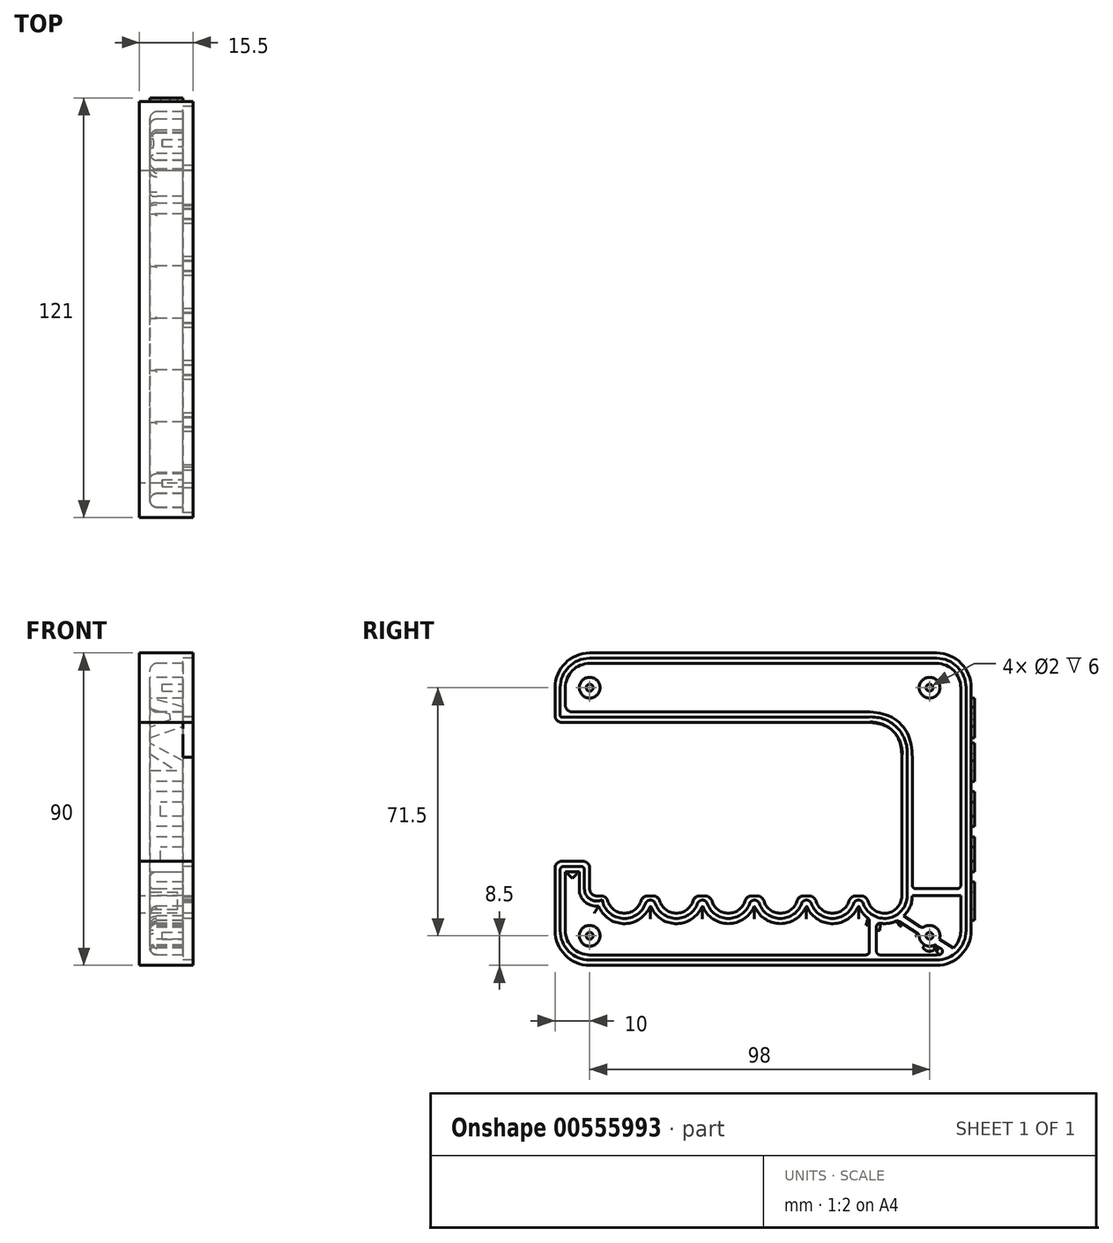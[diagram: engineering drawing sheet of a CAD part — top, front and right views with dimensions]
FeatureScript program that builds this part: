
annotation { "Feature Type Name" : "Feature", "Feature Type Description" : "" }
export const myFeature = defineFeature(function(context is Context, id is Id, definition is map)
    precondition{}
    {
        {
            var Q0;
            Q0=qCreatedBy(makeId("Right.planeOp"),FACE);
            var sketch = newSketch(context, id + "F0", { "sketchPlane" : qUnion([Q0])});
            skLineSegment(sketch, "E0", {"start": v(-120, 0) * mm, "end": v(0, 0) * mm});
            skLineSegment(sketch, "E1", {"start": v(0, 0) * mm, "end": v(0, 90) * mm});
            skLineSegment(sketch, "E2", {"start": v(0, 90) * mm, "end": v(-120, 90) * mm});
            skLineSegment(sketch, "E3", {"start": v(-120, 90) * mm, "end": v(-120, 70) * mm});
            skLineSegment(sketch, "E4", {"start": v(-120, 70) * mm, "end": v(-20, 70) * mm});
            skLineSegment(sketch, "E5", {"start": v(-20, 70) * mm, "end": v(-20, 20) * mm});
            skLineSegment(sketch, "E6", {"start": v(-120, 0) * mm, "end": v(-120, 30) * mm});
            skLineSegment(sketch, "E7", {"start": v(-120, 30) * mm, "end": v(-110, 30) * mm});
            skLineSegment(sketch, "E8", {"start": v(-110, 30) * mm, "end": v(-110, 20) * mm});
            skPoint(sketch, "E9.orphan", {"position": v(-120, 20) * mm});
            skLineSegment(sketch, "E10", {"start": v(-110, 20) * mm, "end": v(-105, 20) * mm});
            skArc(sketch, "E11", {"start": v(-105, 20) * mm, "mid": v(-100, 15) * mm, "end": v(-95, 20) * mm});
            skLineSegment(sketch, "E12", {"start": v(-95, 20) * mm, "end": v(-90, 20) * mm});
            skArc(sketch, "E13", {"start": v(-90, 20) * mm, "mid": v(-85, 15) * mm, "end": v(-80, 20) * mm});
            skLineSegment(sketch, "E14", {"start": v(-80, 20) * mm, "end": v(-75, 20) * mm});
            skArc(sketch, "E15", {"start": v(-75, 20) * mm, "mid": v(-70, 15) * mm, "end": v(-65, 20) * mm});
            skLineSegment(sketch, "E16", {"start": v(-65, 20) * mm, "end": v(-60, 20) * mm});
            skArc(sketch, "E17", {"start": v(-60, 20) * mm, "mid": v(-55, 15) * mm, "end": v(-50, 20) * mm});
            skLineSegment(sketch, "E18", {"start": v(-50, 20) * mm, "end": v(-45, 20) * mm});
            skArc(sketch, "E19", {"start": v(-45, 20) * mm, "mid": v(-40, 15) * mm, "end": v(-35, 20) * mm});
            skLineSegment(sketch, "E20", {"start": v(-35, 20) * mm, "end": v(-30, 20) * mm});
            skArc(sketch, "E21", {"start": v(-30, 20) * mm, "mid": v(-25, 15) * mm, "end": v(-20, 20) * mm});
            skSolve(sketch);
        }
        {
            var Q0;
            Q0=makeQuery(id+"F0.imprint","IMPRINT",FACE,{"disambiguationData":[TD([[makeQuery(id+"F0.imprint","IMPRINT",EDGE,{"derivedFrom":sQuery(id+"F0.wireOp",EDGE,"E0")}),1.0]])]});
            extrude(context, id + "F1", {"entities" : qUnion([Q0]), "depth" : 12.5 * mm, "offsetDistance" : 25 * mm});
        }
        {
            var Q0;
            Q0=makeQuery(id+"F1.opExtrude","SWEPT_EDGE",EDGE,{"disambiguationData":[OSD([sQuery(id+"F0.wireOp",EDGE,"E2"),sQuery(id+"F0.wireOp",EDGE,"E3")])]});
            var Q1;
            Q1=makeQuery(id+"F1.opExtrude","SWEPT_EDGE",EDGE,{"disambiguationData":[OSD([sQuery(id+"F0.wireOp",EDGE,"E1"),sQuery(id+"F0.wireOp",EDGE,"E2")])]});
            var Q2;
            Q2=makeQuery(id+"F1.opExtrude","SWEPT_EDGE",EDGE,{"disambiguationData":[OSD([sQuery(id+"F0.wireOp",EDGE,"E0"),sQuery(id+"F0.wireOp",EDGE,"E1")])]});
            var Q3;
            Q3=makeQuery(id+"F1.opExtrude","SWEPT_EDGE",EDGE,{"disambiguationData":[OSD([sQuery(id+"F0.wireOp",EDGE,"E0"),sQuery(id+"F0.wireOp",EDGE,"E6")])]});
            fillet(context, id + "F2", {"entities" : qUnion([Q0, Q1, Q2, Q3]), "radius" : 10 * mm, "tangentPropagation" : true, "allowEdgeOverflow" : false});
        }
        {
            var Q0;
            Q0=makeQuery(id+"F1.opExtrude","SWEPT_EDGE",EDGE,{"disambiguationData":[OSD([sQuery(id+"F0.wireOp",EDGE,"E4"),sQuery(id+"F0.wireOp",EDGE,"E5")])]});
            fillet(context, id + "F3", {"entities" : qUnion([Q0]), "radius" : 10 * mm, "tangentPropagation" : true, "rho" : 0.5, "crossSection" : FilletCrossSection.CONIC, "allowEdgeOverflow" : false});
        }
        {
            var Q0;
            Q0=makeQuery(id+"F1.opExtrude","SWEPT_EDGE",EDGE,{"disambiguationData":[OSD([sQuery(id+"F0.wireOp",EDGE,"E6"),sQuery(id+"F0.wireOp",EDGE,"E7")])]});
            var Q1;
            Q1=makeQuery(id+"F1.opExtrude","SWEPT_EDGE",EDGE,{"disambiguationData":[OSD([sQuery(id+"F0.wireOp",EDGE,"E7"),sQuery(id+"F0.wireOp",EDGE,"E8")])]});
            var Q2;
            Q2=makeQuery(id+"F1.opExtrude","SWEPT_EDGE",EDGE,{"disambiguationData":[OSD([sQuery(id+"F0.wireOp",EDGE,"E8"),sQuery(id+"F0.wireOp",EDGE,"E10")])]});
            var Q3;
            Q3=makeQuery(id+"F1.opExtrude","SWEPT_EDGE",EDGE,{"disambiguationData":[OSD([sQuery(id+"F0.wireOp",EDGE,"E10"),sQuery(id+"F0.wireOp",EDGE,"E11")])]});
            var Q4;
            Q4=makeQuery(id+"F1.opExtrude","SWEPT_EDGE",EDGE,{"disambiguationData":[OSD([sQuery(id+"F0.wireOp",EDGE,"E11"),sQuery(id+"F0.wireOp",EDGE,"E12")])]});
            var Q5;
            Q5=makeQuery(id+"F1.opExtrude","SWEPT_EDGE",EDGE,{"disambiguationData":[OSD([sQuery(id+"F0.wireOp",EDGE,"E12"),sQuery(id+"F0.wireOp",EDGE,"E13")])]});
            var Q6;
            Q6=makeQuery(id+"F1.opExtrude","SWEPT_EDGE",EDGE,{"disambiguationData":[OSD([sQuery(id+"F0.wireOp",EDGE,"E13"),sQuery(id+"F0.wireOp",EDGE,"E14")])]});
            var Q7;
            Q7=makeQuery(id+"F1.opExtrude","SWEPT_EDGE",EDGE,{"disambiguationData":[OSD([sQuery(id+"F0.wireOp",EDGE,"E14"),sQuery(id+"F0.wireOp",EDGE,"E15")])]});
            var Q8;
            Q8=makeQuery(id+"F1.opExtrude","SWEPT_EDGE",EDGE,{"disambiguationData":[OSD([sQuery(id+"F0.wireOp",EDGE,"E15"),sQuery(id+"F0.wireOp",EDGE,"E16")])]});
            var Q9;
            Q9=makeQuery(id+"F1.opExtrude","SWEPT_EDGE",EDGE,{"disambiguationData":[OSD([sQuery(id+"F0.wireOp",EDGE,"E16"),sQuery(id+"F0.wireOp",EDGE,"E17")])]});
            var Q10;
            Q10=makeQuery(id+"F1.opExtrude","SWEPT_EDGE",EDGE,{"disambiguationData":[OSD([sQuery(id+"F0.wireOp",EDGE,"E17"),sQuery(id+"F0.wireOp",EDGE,"E18")])]});
            var Q11;
            Q11=makeQuery(id+"F1.opExtrude","SWEPT_EDGE",EDGE,{"disambiguationData":[OSD([sQuery(id+"F0.wireOp",EDGE,"E18"),sQuery(id+"F0.wireOp",EDGE,"E19")])]});
            var Q12;
            Q12=makeQuery(id+"F1.opExtrude","SWEPT_EDGE",EDGE,{"disambiguationData":[OSD([sQuery(id+"F0.wireOp",EDGE,"E19"),sQuery(id+"F0.wireOp",EDGE,"E20")])]});
            var Q13;
            Q13=makeQuery(id+"F1.opExtrude","SWEPT_EDGE",EDGE,{"disambiguationData":[OSD([sQuery(id+"F0.wireOp",EDGE,"E20"),sQuery(id+"F0.wireOp",EDGE,"E21")])]});
            fillet(context, id + "F4", {"entities" : qUnion([Q0, Q1, Q2, Q3, Q4, Q5, Q6, Q7, Q8, Q9, Q10, Q11, Q12, Q13]), "radius" : 2 * mm, "tangentPropagation" : true, "allowEdgeOverflow" : false});
        }
        {
            var Q0;
            Q0=makeQuery(id+"F1.opExtrude","SWEPT_FACE",FACE,{"disambiguationData":[OSD([sQuery(id+"F0.wireOp",EDGE,"E1")])]});
            var sketch = newSketch(context, id + "F5", { "sketchPlane" : qUnion([Q0])});
            skLineSegment(sketch, "E22.bottom", {"start": v(-12.5, 13) * mm, "end": v(-3, 13) * mm, "construction": true});
            skLineSegment(sketch, "E22.top", {"start": v(-12.5, 77) * mm, "end": v(-3, 77) * mm, "construction": true});
            skLineSegment(sketch, "E22.right", {"start": v(-3, 13) * mm, "end": v(-3, 77) * mm, "construction": true});
            skLineSegment(sketch, "E23.bottom", {"start": v(-12.5, 13) * mm, "end": v(-3, 13) * mm});
            skLineSegment(sketch, "E23.right", {"start": v(-3, 13) * mm, "end": v(-3, 16) * mm});
            skLineSegment(sketch, "E24.right", {"start": v(-11, 16) * mm, "end": v(-11, 21) * mm});
            skLineSegment(sketch, "E25.top", {"start": v(-12.5, 24) * mm, "end": v(-3, 24) * mm});
            skLineSegment(sketch, "E25.right", {"start": v(-3, 21) * mm, "end": v(-3, 24) * mm});
            skLineSegment(sketch, "E26.trimOffspring", {"start": v(-11, 21) * mm, "end": v(-3, 21) * mm});
            skLineSegment(sketch, "E27.trimOffspring", {"start": v(-11, 16) * mm, "end": v(-3, 16) * mm});
            skLineSegment(sketch, "E28.top", {"start": v(-12.5, 37) * mm, "end": v(-3, 37) * mm});
            skLineSegment(sketch, "E28.right", {"start": v(-3, 27) * mm, "end": v(-3, 37) * mm});
            skLineSegment(sketch, "E29.bottom", {"start": v(-12.5, 40) * mm, "end": v(-3, 40) * mm});
            skLineSegment(sketch, "E29.top", {"start": v(-12.5, 50) * mm, "end": v(-3, 50) * mm});
            skLineSegment(sketch, "E29.right", {"start": v(-3, 40) * mm, "end": v(-3, 50) * mm});
            skLineSegment(sketch, "E30.bottom", {"start": v(-12.5, 30) * mm, "end": v(-6, 30) * mm});
            skLineSegment(sketch, "E30.top", {"start": v(-12.5, 34) * mm, "end": v(-6, 34) * mm});
            skLineSegment(sketch, "E30.right", {"start": v(-6, 30) * mm, "end": v(-6, 34) * mm});
            skLineSegment(sketch, "E31.bottom", {"start": v(-12.5, 43) * mm, "end": v(-6, 43) * mm});
            skLineSegment(sketch, "E31.top", {"start": v(-12.5, 47) * mm, "end": v(-6, 47) * mm});
            skLineSegment(sketch, "E31.right", {"start": v(-6, 43) * mm, "end": v(-6, 47) * mm});
            skLineSegment(sketch, "E32.bottom", {"start": v(-12.5, 53) * mm, "end": v(-3, 53) * mm});
            skLineSegment(sketch, "E32.right", {"start": v(-3, 53) * mm, "end": v(-3, 56) * mm});
            skLineSegment(sketch, "E33", {"start": v(-12.5, 59) * mm, "end": v(-3, 64) * mm});
            skLineSegment(sketch, "E34", {"start": v(-3, 64) * mm, "end": v(-3, 61) * mm});
            skLineSegment(sketch, "E35", {"start": v(-3, 65.61) * mm, "end": v(-12.5, 68.8) * mm});
            skLineSegment(sketch, "E36", {"start": v(-12.5, 74.5) * mm, "end": v(-3, 77) * mm});
            skLineSegment(sketch, "E37", {"start": v(-8.81, 70.73) * mm, "end": v(-3, 68.61) * mm});
            skLineSegment(sketch, "E38", {"start": v(-3, 68.61) * mm, "end": v(-3, 65.61) * mm});
            skLineSegment(sketch, "E39", {"start": v(-3, 77) * mm, "end": v(-3, 74) * mm});
            skLineSegment(sketch, "E40", {"start": v(-3, 74) * mm, "end": v(-8.57, 72.5) * mm});
            skLineSegment(sketch, "E41", {"start": v(-8.57, 72.5) * mm, "end": v(-8.81, 70.73) * mm});
            skLineSegment(sketch, "E42", {"start": v(-3, 61) * mm, "end": v(-10.73, 56) * mm});
            skLineSegment(sketch, "E43.trimOffspring", {"start": v(-10.73, 56) * mm, "end": v(-3, 56) * mm});
            skLineSegment(sketch, "E44", {"start": v(-12.5, 74.5) * mm, "end": v(-12.5, 68.8) * mm});
            skLineSegment(sketch, "E45.trimOffspring", {"start": v(-12.5, 59) * mm, "end": v(-12.5, 53) * mm});
            skPoint(sketch, "E32.top.end.orphan", {"position": v(-12.5, 56) * mm});
            skPoint(sketch, "E25.bottom.end.orphan", {"position": v(-14, 21) * mm});
            skLineSegment(sketch, "E46", {"start": v(-3, 27) * mm, "end": v(-12.5, 27) * mm});
            skLineSegment(sketch, "E47.trimOffspring", {"start": v(-12.5, 24) * mm, "end": v(-12.5, 13) * mm});
            skLineSegment(sketch, "E48.trimOffspring", {"start": v(-12.5, 30) * mm, "end": v(-12.5, 27) * mm});
            skLineSegment(sketch, "E49.trimOffspring", {"start": v(-12.5, 37) * mm, "end": v(-12.5, 34) * mm});
            skLineSegment(sketch, "E50.trimOffspring", {"start": v(-12.5, 43) * mm, "end": v(-12.5, 40) * mm});
            skLineSegment(sketch, "E51.trimOffspring", {"start": v(-12.5, 50) * mm, "end": v(-12.5, 47) * mm});
            skSolve(sketch);
        }
        {
            var Q0;
            Q0 = qSketchRegion(id + "F5", true);
            extrude(context, id + "F6", {"entities" : qUnion([Q0]), "operationType" : NewBodyOperationType.ADD, "depth" : 1 * mm, "offsetDistance" : 25 * mm});
        }
        {
            var Q0;
            Q0=makeQuery(id+"F6.boolean.opBoolean","MERGE",FACE,{"derivedFrom":[makeQuery(id+"F1.opExtrude","CAP_FACE",FACE,{"disambiguationData":[OSD([sQuery(id+"F0.wireOp",EDGE,"E0"),sQuery(id+"F0.wireOp",EDGE,"E1"),sQuery(id+"F0.wireOp",EDGE,"E2"),sQuery(id+"F0.wireOp",EDGE,"E3"),sQuery(id+"F0.wireOp",EDGE,"E4"),sQuery(id+"F0.wireOp",EDGE,"E5"),sQuery(id+"F0.wireOp",EDGE,"E6"),sQuery(id+"F0.wireOp",EDGE,"E7"),sQuery(id+"F0.wireOp",EDGE,"E8"),sQuery(id+"F0.wireOp",EDGE,"E10"),sQuery(id+"F0.wireOp",EDGE,"E11"),sQuery(id+"F0.wireOp",EDGE,"E12"),sQuery(id+"F0.wireOp",EDGE,"E13"),sQuery(id+"F0.wireOp",EDGE,"E14"),sQuery(id+"F0.wireOp",EDGE,"E15"),sQuery(id+"F0.wireOp",EDGE,"E16"),sQuery(id+"F0.wireOp",EDGE,"E17"),sQuery(id+"F0.wireOp",EDGE,"E18"),sQuery(id+"F0.wireOp",EDGE,"E19"),sQuery(id+"F0.wireOp",EDGE,"E20"),sQuery(id+"F0.wireOp",EDGE,"E21")])],"isStart":false}),makeQuery(id+"F6.opExtrude","SWEPT_FACE",FACE,{"disambiguationData":[OSD([sQuery(id+"F5.wireOp",EDGE,"E44")])]}),makeQuery(id+"F6.opExtrude","SWEPT_FACE",FACE,{"disambiguationData":[OSD([sQuery(id+"F5.wireOp",EDGE,"E45.trimOffspring")])]}),makeQuery(id+"F6.opExtrude","SWEPT_FACE",FACE,{"disambiguationData":[OSD([sQuery(id+"F5.wireOp",EDGE,"E47.trimOffspring")])]}),makeQuery(id+"F6.opExtrude","SWEPT_FACE",FACE,{"disambiguationData":[OSD([sQuery(id+"F5.wireOp",EDGE,"E48.trimOffspring")])]}),makeQuery(id+"F6.opExtrude","SWEPT_FACE",FACE,{"disambiguationData":[OSD([sQuery(id+"F5.wireOp",EDGE,"E49.trimOffspring")])]}),makeQuery(id+"F6.opExtrude","SWEPT_FACE",FACE,{"disambiguationData":[OSD([sQuery(id+"F5.wireOp",EDGE,"E50.trimOffspring")])]}),makeQuery(id+"F6.opExtrude","SWEPT_FACE",FACE,{"disambiguationData":[OSD([sQuery(id+"F5.wireOp",EDGE,"E51.trimOffspring")])]})]});
            shell(context, id + "F7", {"entities" : qUnion([Q0]), "thickness" : 3 * mm});
        }
        {
            var Q0;
            Q0=makeQuery(id+"F1.opExtrude","SWEPT_EDGE",EDGE,{"disambiguationData":[OSD([sQuery(id+"F0.wireOp",EDGE,"E3"),sQuery(id+"F0.wireOp",EDGE,"E4")])]});
            fillet(context, id + "F8", {"entities" : qUnion([Q0]), "radius" : 2 * mm, "tangentPropagation" : true, "allowEdgeOverflow" : false});
        }
        {
            var Q0;
            Q0=makeQuery(id+"F7.opShell","OFFSET_EDGE",EDGE,{"disambiguationData":[OSD([sQuery(id+"F0.wireOp",EDGE,"E3"),sQuery(id+"F0.wireOp",EDGE,"E4")])]});
            var Q1;
            {var subQ0=sQuery(id+"F0.wireOp",EDGE,"E4");Q1=makeQuery(id+"F7.opShell","OFFSET_EDGE",EDGE,{"disambiguationData":[OSD([subQ0]),TDD([makeQuery(id+"F1.opExtrude","CAP_EDGE",EDGE,{"disambiguationData":[OSD([subQ0])],"isStart":true})])]});}
            var Q2;
            {var subQ0=sQuery(id+"F0.wireOp",EDGE,"E21");var subQ1=sQuery(id+"F0.wireOp",EDGE,"E20");var subQ2=sQuery(id+"F0.wireOp",EDGE,"E19");var subQ3=sQuery(id+"F0.wireOp",EDGE,"E18");var subQ4=sQuery(id+"F0.wireOp",EDGE,"E17");var subQ5=sQuery(id+"F0.wireOp",EDGE,"E16");var subQ6=sQuery(id+"F0.wireOp",EDGE,"E15");var subQ7=sQuery(id+"F0.wireOp",EDGE,"E14");var subQ8=sQuery(id+"F0.wireOp",EDGE,"E13");var subQ9=sQuery(id+"F0.wireOp",EDGE,"E12");var subQ10=sQuery(id+"F0.wireOp",EDGE,"E11");var subQ11=sQuery(id+"F0.wireOp",EDGE,"E10");var subQ12=sQuery(id+"F0.wireOp",EDGE,"E8");var subQ13=sQuery(id+"F0.wireOp",EDGE,"E7");var subQ14=sQuery(id+"F0.wireOp",EDGE,"E6");var subQ15=sQuery(id+"F0.wireOp",EDGE,"E5");var subQ16=sQuery(id+"F0.wireOp",EDGE,"E4");var subQ17=sQuery(id+"F0.wireOp",EDGE,"E3");var subQ18=sQuery(id+"F0.wireOp",EDGE,"E2");var subQ19=sQuery(id+"F0.wireOp",EDGE,"E1");var subQ20=sQuery(id+"F0.wireOp",EDGE,"E0");Q2=makeQuery(id+"F7.opShell","OFFSET_EDGE",EDGE,{"disambiguationData":[OSD([subQ20,subQ19,subQ18,subQ17,subQ16,subQ15,subQ14,subQ13,subQ12,subQ11,subQ10,subQ9,subQ8,subQ7,subQ6,subQ5,subQ4,subQ3,subQ2,subQ1,subQ0]),TDD([makeQuery(id+"F3.opFillet","BLEND_EDGE",EDGE,{"blendedFrom":[makeQuery(id+"F1.opExtrude","SWEPT_EDGE",EDGE,{"disambiguationData":[OSD([subQ16,subQ15])]}),makeQuery(id+"F1.opExtrude","CAP_FACE",FACE,{"disambiguationData":[OSD([subQ20,subQ19,subQ18,subQ17,subQ16,subQ15,subQ14,subQ13,subQ12,subQ11,subQ10,subQ9,subQ8,subQ7,subQ6,subQ5,subQ4,subQ3,subQ2,subQ1,subQ0])],"isStart":true})],"blendedInto":[makeQuery(id+"F1.opExtrude","CAP_FACE",FACE,{"disambiguationData":[OSD([subQ20,subQ19,subQ18,subQ17,subQ16,subQ15,subQ14,subQ13,subQ12,subQ11,subQ10,subQ9,subQ8,subQ7,subQ6,subQ5,subQ4,subQ3,subQ2,subQ1,subQ0])],"isStart":true})]})])]});}
            var Q3;
            {var subQ0=sQuery(id+"F0.wireOp",EDGE,"E19");Q3=makeQuery(id+"F7.opShell","OFFSET_EDGE",EDGE,{"disambiguationData":[OSD([subQ0]),TDD([makeQuery(id+"F1.opExtrude","CAP_EDGE",EDGE,{"disambiguationData":[OSD([subQ0])],"isStart":true})])]});}
            var Q4;
            {var subQ0=sQuery(id+"F0.wireOp",EDGE,"E17");Q4=makeQuery(id+"F7.opShell","OFFSET_EDGE",EDGE,{"disambiguationData":[OSD([subQ0]),TDD([makeQuery(id+"F1.opExtrude","CAP_EDGE",EDGE,{"disambiguationData":[OSD([subQ0])],"isStart":true})])]});}
            var Q5;
            {var subQ0=sQuery(id+"F0.wireOp",EDGE,"E15");Q5=makeQuery(id+"F7.opShell","OFFSET_EDGE",EDGE,{"disambiguationData":[OSD([subQ0]),TDD([makeQuery(id+"F1.opExtrude","CAP_EDGE",EDGE,{"disambiguationData":[OSD([subQ0])],"isStart":true})])]});}
            var Q6;
            {var subQ0=sQuery(id+"F0.wireOp",EDGE,"E13");Q6=makeQuery(id+"F7.opShell","OFFSET_EDGE",EDGE,{"disambiguationData":[OSD([subQ0]),TDD([makeQuery(id+"F1.opExtrude","CAP_EDGE",EDGE,{"disambiguationData":[OSD([subQ0])],"isStart":true})])]});}
            var Q7;
            {var subQ0=sQuery(id+"F0.wireOp",EDGE,"E11");Q7=makeQuery(id+"F7.opShell","OFFSET_EDGE",EDGE,{"disambiguationData":[OSD([subQ0]),TDD([makeQuery(id+"F1.opExtrude","CAP_EDGE",EDGE,{"disambiguationData":[OSD([subQ0])],"isStart":true})])]});}
            var Q8;
            {var subQ0=sQuery(id+"F0.wireOp",EDGE,"E21");var subQ1=sQuery(id+"F0.wireOp",EDGE,"E20");var subQ2=sQuery(id+"F0.wireOp",EDGE,"E19");var subQ3=sQuery(id+"F0.wireOp",EDGE,"E18");var subQ4=sQuery(id+"F0.wireOp",EDGE,"E17");var subQ5=sQuery(id+"F0.wireOp",EDGE,"E16");var subQ6=sQuery(id+"F0.wireOp",EDGE,"E15");var subQ7=sQuery(id+"F0.wireOp",EDGE,"E14");var subQ8=sQuery(id+"F0.wireOp",EDGE,"E13");var subQ9=sQuery(id+"F0.wireOp",EDGE,"E12");var subQ10=sQuery(id+"F0.wireOp",EDGE,"E11");var subQ11=sQuery(id+"F0.wireOp",EDGE,"E10");var subQ12=sQuery(id+"F0.wireOp",EDGE,"E8");var subQ13=sQuery(id+"F0.wireOp",EDGE,"E7");var subQ14=sQuery(id+"F0.wireOp",EDGE,"E6");var subQ15=sQuery(id+"F0.wireOp",EDGE,"E5");var subQ16=sQuery(id+"F0.wireOp",EDGE,"E4");var subQ17=sQuery(id+"F0.wireOp",EDGE,"E3");var subQ18=sQuery(id+"F0.wireOp",EDGE,"E2");var subQ19=sQuery(id+"F0.wireOp",EDGE,"E1");var subQ20=sQuery(id+"F0.wireOp",EDGE,"E0");Q8=makeQuery(id+"F7.opShell","OFFSET_EDGE",EDGE,{"disambiguationData":[OSD([subQ20,subQ19,subQ18,subQ17,subQ16,subQ15,subQ14,subQ13,subQ12,subQ11,subQ10,subQ9,subQ8,subQ7,subQ6,subQ5,subQ4,subQ3,subQ2,subQ1,subQ0]),TDD([makeQuery(id+"F4.opFillet","BLEND_EDGE",EDGE,{"blendedFrom":[makeQuery(id+"F1.opExtrude","SWEPT_EDGE",EDGE,{"disambiguationData":[OSD([subQ12,subQ11])]}),makeQuery(id+"F1.opExtrude","CAP_FACE",FACE,{"disambiguationData":[OSD([subQ20,subQ19,subQ18,subQ17,subQ16,subQ15,subQ14,subQ13,subQ12,subQ11,subQ10,subQ9,subQ8,subQ7,subQ6,subQ5,subQ4,subQ3,subQ2,subQ1,subQ0])],"isStart":true})],"blendedInto":[makeQuery(id+"F1.opExtrude","CAP_FACE",FACE,{"disambiguationData":[OSD([subQ20,subQ19,subQ18,subQ17,subQ16,subQ15,subQ14,subQ13,subQ12,subQ11,subQ10,subQ9,subQ8,subQ7,subQ6,subQ5,subQ4,subQ3,subQ2,subQ1,subQ0])],"isStart":true})]})])]});}
            var Q9;
            {var subQ0=sQuery(id+"F0.wireOp",EDGE,"E7");Q9=makeQuery(id+"F7.opShell","OFFSET_EDGE",EDGE,{"disambiguationData":[OSD([subQ0]),TDD([makeQuery(id+"F1.opExtrude","CAP_EDGE",EDGE,{"disambiguationData":[OSD([subQ0])],"isStart":true})])]});}
            var Q10;
            {var subQ0=sQuery(id+"F0.wireOp",EDGE,"E2");Q10=makeQuery(id+"F7.opShell","OFFSET_EDGE",EDGE,{"disambiguationData":[OSD([subQ0]),TDD([makeQuery(id+"F1.opExtrude","CAP_EDGE",EDGE,{"disambiguationData":[OSD([subQ0])],"isStart":true})])]});}
            fillet(context, id + "F9", {"entities" : qUnion([Q0, Q1, Q2, Q3, Q4, Q5, Q6, Q7, Q8, Q9, Q10]), "radius" : 2 * mm, "tangentPropagation" : true, "allowEdgeOverflow" : false});
        }
        {
            var Q0;
            Q0=makeQuery(id+"F7.opShell","OFFSET_EDGE",EDGE,{"disambiguationData":[OSD([sQuery(id+"F0.wireOp",EDGE,"E19"),sQuery(id+"F0.wireOp",EDGE,"E20")])]});
            var Q1;
            Q1=makeQuery(id+"F7.opShell","OFFSET_EDGE",EDGE,{"disambiguationData":[OSD([sQuery(id+"F0.wireOp",EDGE,"E17"),sQuery(id+"F0.wireOp",EDGE,"E18")])]});
            var Q2;
            Q2=makeQuery(id+"F7.opShell","OFFSET_EDGE",EDGE,{"disambiguationData":[OSD([sQuery(id+"F0.wireOp",EDGE,"E16"),sQuery(id+"F0.wireOp",EDGE,"E17")])]});
            var Q3;
            Q3=makeQuery(id+"F7.opShell","OFFSET_EDGE",EDGE,{"disambiguationData":[OSD([sQuery(id+"F0.wireOp",EDGE,"E13"),sQuery(id+"F0.wireOp",EDGE,"E14")])]});
            var Q4;
            Q4=makeQuery(id+"F7.opShell","OFFSET_EDGE",EDGE,{"disambiguationData":[OSD([sQuery(id+"F0.wireOp",EDGE,"E11"),sQuery(id+"F0.wireOp",EDGE,"E12")])]});
            fillet(context, id + "F10", {"entities" : qUnion([Q0, Q1, Q2, Q3, Q4]), "radius" : 3 * mm, "tangentPropagation" : true, "allowEdgeOverflow" : false});
        }
        {
            var Q0;
            Q0=makeQuery(id+"F7.opShell","OFFSET_FACE",FACE,{"disambiguationData":[OSD([sQuery(id+"F0.wireOp",EDGE,"E0"),sQuery(id+"F0.wireOp",EDGE,"E1"),sQuery(id+"F0.wireOp",EDGE,"E2"),sQuery(id+"F0.wireOp",EDGE,"E3"),sQuery(id+"F0.wireOp",EDGE,"E4"),sQuery(id+"F0.wireOp",EDGE,"E5"),sQuery(id+"F0.wireOp",EDGE,"E6"),sQuery(id+"F0.wireOp",EDGE,"E7"),sQuery(id+"F0.wireOp",EDGE,"E8"),sQuery(id+"F0.wireOp",EDGE,"E10"),sQuery(id+"F0.wireOp",EDGE,"E11"),sQuery(id+"F0.wireOp",EDGE,"E12"),sQuery(id+"F0.wireOp",EDGE,"E13"),sQuery(id+"F0.wireOp",EDGE,"E14"),sQuery(id+"F0.wireOp",EDGE,"E15"),sQuery(id+"F0.wireOp",EDGE,"E16"),sQuery(id+"F0.wireOp",EDGE,"E17"),sQuery(id+"F0.wireOp",EDGE,"E18"),sQuery(id+"F0.wireOp",EDGE,"E19"),sQuery(id+"F0.wireOp",EDGE,"E20"),sQuery(id+"F0.wireOp",EDGE,"E21")])]});
            var sketch = newSketch(context, id + "F11", { "sketchPlane" : qUnion([Q0])});
            skLineSegment(sketch, "E52", {"start": v(-5.31, 2.66) * mm, "end": v(-21.96, 13.39) * mm});
            skLineSegment(sketch, "E53.0", {"start": v(-4.23, 4.34) * mm, "end": v(-20.87, 15.07) * mm});
            skLineSegment(sketch, "E54", {"start": v(-21.96, 13.39) * mm, "end": v(-20.87, 15.07) * mm});
            skLineSegment(sketch, "E55", {"start": v(-5.31, 2.66) * mm, "end": v(-4.23, 4.34) * mm});
            skLineSegment(sketch, "E56", {"start": v(-19.5, 20.07) * mm, "end": v(-1.44, 20.07) * mm});
            skLineSegment(sketch, "E57.0", {"start": v(-19.5, 22.07) * mm, "end": v(-1.44, 22.07) * mm});
            skLineSegment(sketch, "E58", {"start": v(-19.5, 22.07) * mm, "end": v(-19.5, 20.07) * mm});
            skLineSegment(sketch, "E59", {"start": v(-1.44, 22.07) * mm, "end": v(-1.44, 20.07) * mm});
            skLineSegment(sketch, "E60.bottom", {"start": v(-29.33, 14) * mm, "end": v(-27.33, 14) * mm});
            skLineSegment(sketch, "E60.top", {"start": v(-29.33, 2) * mm, "end": v(-27.33, 2) * mm});
            skLineSegment(sketch, "E60.left", {"start": v(-29.33, 14) * mm, "end": v(-29.33, 2) * mm});
            skLineSegment(sketch, "E60.right", {"start": v(-27.33, 14) * mm, "end": v(-27.33, 2) * mm});
            skLineSegment(sketch, "E61", {"start": v(-120.44, 45) * mm, "end": v(50.04, 45) * mm, "construction": true});
            skSolve(sketch);
        }
        {
            var Q0;
            Q0 = qSketchRegion(id + "F11", true);
            extrude(context, id + "F12", {"entities" : qUnion([Q0]), "operationType" : NewBodyOperationType.ADD, "depth" : 9.5 * mm, "offsetDistance" : 25 * mm});
        }
        {
            var Q0;
            Q0=makeQuery(id+"F6.boolean.opBoolean","MERGE",FACE,{"derivedFrom":[makeQuery(id+"F1.opExtrude","CAP_FACE",FACE,{"disambiguationData":[OSD([sQuery(id+"F0.wireOp",EDGE,"E0"),sQuery(id+"F0.wireOp",EDGE,"E1"),sQuery(id+"F0.wireOp",EDGE,"E2"),sQuery(id+"F0.wireOp",EDGE,"E3"),sQuery(id+"F0.wireOp",EDGE,"E4"),sQuery(id+"F0.wireOp",EDGE,"E5"),sQuery(id+"F0.wireOp",EDGE,"E6"),sQuery(id+"F0.wireOp",EDGE,"E7"),sQuery(id+"F0.wireOp",EDGE,"E8"),sQuery(id+"F0.wireOp",EDGE,"E10"),sQuery(id+"F0.wireOp",EDGE,"E11"),sQuery(id+"F0.wireOp",EDGE,"E12"),sQuery(id+"F0.wireOp",EDGE,"E13"),sQuery(id+"F0.wireOp",EDGE,"E14"),sQuery(id+"F0.wireOp",EDGE,"E15"),sQuery(id+"F0.wireOp",EDGE,"E16"),sQuery(id+"F0.wireOp",EDGE,"E17"),sQuery(id+"F0.wireOp",EDGE,"E18"),sQuery(id+"F0.wireOp",EDGE,"E19"),sQuery(id+"F0.wireOp",EDGE,"E20"),sQuery(id+"F0.wireOp",EDGE,"E21")])],"isStart":false}),makeQuery(id+"F6.opExtrude","SWEPT_FACE",FACE,{"disambiguationData":[OSD([sQuery(id+"F5.wireOp",EDGE,"E44")])]}),makeQuery(id+"F6.opExtrude","SWEPT_FACE",FACE,{"disambiguationData":[OSD([sQuery(id+"F5.wireOp",EDGE,"E45.trimOffspring")])]}),makeQuery(id+"F6.opExtrude","SWEPT_FACE",FACE,{"disambiguationData":[OSD([sQuery(id+"F5.wireOp",EDGE,"E47.trimOffspring")])]}),makeQuery(id+"F6.opExtrude","SWEPT_FACE",FACE,{"disambiguationData":[OSD([sQuery(id+"F5.wireOp",EDGE,"E48.trimOffspring")])]}),makeQuery(id+"F6.opExtrude","SWEPT_FACE",FACE,{"disambiguationData":[OSD([sQuery(id+"F5.wireOp",EDGE,"E49.trimOffspring")])]}),makeQuery(id+"F6.opExtrude","SWEPT_FACE",FACE,{"disambiguationData":[OSD([sQuery(id+"F5.wireOp",EDGE,"E50.trimOffspring")])]}),makeQuery(id+"F6.opExtrude","SWEPT_FACE",FACE,{"disambiguationData":[OSD([sQuery(id+"F5.wireOp",EDGE,"E51.trimOffspring")])]})]});
            var sketch = newSketch(context, id + "F13", { "sketchPlane" : qUnion([Q0])});
            skLineSegment(sketch, "E62", {"start": v(-10, 90) * mm, "end": v(-110, 90) * mm});
            skArc(sketch, "E63", {"start": v(-110, 90) * mm, "mid": v(-117.07, 87.07) * mm, "end": v(-120, 80) * mm});
            skArc(sketch, "E64", {"start": v(-120, 72) * mm, "mid": v(-119.41, 70.59) * mm, "end": v(-118, 70) * mm});
            skLineSegment(sketch, "E65", {"start": v(-120, 80) * mm, "end": v(-120, 72) * mm});
            skLineSegment(sketch, "E66", {"start": v(-30, 70) * mm, "end": v(-118, 70) * mm});
            skLineSegment(sketch, "E67", {"start": v(-20, 60) * mm, "end": v(-20, 20) * mm});
            skArc(sketch, "E68", {"start": v(-20, 60) * mm, "mid": v(-22.51, 67.49) * mm, "end": v(-30, 70) * mm});
            skArc(sketch, "E69", {"start": v(-29.8, 18.58) * mm, "mid": v(-24.28, 15.06) * mm, "end": v(-20, 20) * mm});
            skArc(sketch, "E70", {"start": v(-29.8, 18.58) * mm, "mid": v(-32.5, 20.28) * mm, "end": v(-35.2, 18.58) * mm});
            skArc(sketch, "E71", {"start": v(-44.8, 18.58) * mm, "mid": v(-40, 15) * mm, "end": v(-35.2, 18.58) * mm});
            skArc(sketch, "E72", {"start": v(-44.8, 18.58) * mm, "mid": v(-47.5, 20.28) * mm, "end": v(-50.2, 18.57) * mm});
            skArc(sketch, "E73", {"start": v(-59.8, 18.57) * mm, "mid": v(-55, 15) * mm, "end": v(-50.2, 18.57) * mm});
            skArc(sketch, "E74", {"start": v(-59.8, 18.57) * mm, "mid": v(-62.5, 20.28) * mm, "end": v(-65.2, 18.57) * mm});
            skArc(sketch, "E75", {"start": v(-74.8, 18.57) * mm, "mid": v(-70, 15) * mm, "end": v(-65.2, 18.57) * mm});
            skArc(sketch, "E76", {"start": v(-74.8, 18.57) * mm, "mid": v(-77.5, 20.28) * mm, "end": v(-80.2, 18.57) * mm});
            skArc(sketch, "E77", {"start": v(-89.8, 18.57) * mm, "mid": v(-85, 15) * mm, "end": v(-80.2, 18.57) * mm});
            skArc(sketch, "E78", {"start": v(-89.8, 18.57) * mm, "mid": v(-92.5, 20.28) * mm, "end": v(-95.2, 18.57) * mm});
            skArc(sketch, "E79", {"start": v(-104.8, 18.57) * mm, "mid": v(-100, 15) * mm, "end": v(-95.2, 18.57) * mm});
            skArc(sketch, "E80", {"start": v(-105.51, 19.6) * mm, "mid": v(-106.08, 19.9) * mm, "end": v(-106.7, 20) * mm});
            skArc(sketch, "E81", {"start": v(-104.8, 18.57) * mm, "mid": v(-105.1, 19.13) * mm, "end": v(-105.51, 19.6) * mm});
            skLineSegment(sketch, "E82", {"start": v(-106.7, 20) * mm, "end": v(-108, 20) * mm});
            skArc(sketch, "E83", {"start": v(-110, 22) * mm, "mid": v(-109.41, 20.59) * mm, "end": v(-108, 20) * mm});
            skLineSegment(sketch, "E84", {"start": v(-110, 22) * mm, "end": v(-110, 28) * mm});
            skArc(sketch, "E85", {"start": v(-110, 28) * mm, "mid": v(-110.59, 29.42) * mm, "end": v(-112, 30) * mm});
            skLineSegment(sketch, "E86", {"start": v(-112, 30) * mm, "end": v(-118, 30) * mm});
            skArc(sketch, "E87", {"start": v(-118, 30) * mm, "mid": v(-119.41, 29.42) * mm, "end": v(-120, 28) * mm});
            skLineSegment(sketch, "E88", {"start": v(-120, 28) * mm, "end": v(-120, 10) * mm});
            skArc(sketch, "E89", {"start": v(-120, 10) * mm, "mid": v(-117.07, 2.93) * mm, "end": v(-110, 0) * mm});
            skLineSegment(sketch, "E90", {"start": v(-120, 10) * mm, "end": v(-120, 28) * mm});
            skLineSegment(sketch, "E91", {"start": v(-110, 0) * mm, "end": v(-10, 0) * mm});
            skArc(sketch, "E92", {"start": v(-10, 0) * mm, "mid": v(-2.93, 2.93) * mm, "end": v(0, 10) * mm});
            skLineSegment(sketch, "E93", {"start": v(0, 10) * mm, "end": v(0, 80) * mm});
            skArc(sketch, "E94", {"start": v(0, 80) * mm, "mid": v(-2.93, 87.07) * mm, "end": v(-10, 90) * mm});
            skLineSegment(sketch, "E95.0", {"start": v(-10, 88.5) * mm, "end": v(-110, 88.5) * mm});
            skArc(sketch, "E96.0", {"start": v(-1.5, 80) * mm, "mid": v(-3.99, 86.01) * mm, "end": v(-10, 88.5) * mm});
            skLineSegment(sketch, "E97.0", {"start": v(-1.5, 10) * mm, "end": v(-1.5, 80) * mm});
            skArc(sketch, "E98.0", {"start": v(-10, 1.5) * mm, "mid": v(-3.99, 3.99) * mm, "end": v(-1.5, 10) * mm});
            skArc(sketch, "E99.0", {"start": v(-118.5, 10) * mm, "mid": v(-116.01, 3.99) * mm, "end": v(-110, 1.5) * mm});
            skLineSegment(sketch, "E100", {"start": v(-110, 1.5) * mm, "end": v(-10, 1.5) * mm});
            skLineSegment(sketch, "E101.0", {"start": v(-111.5, 22) * mm, "end": v(-111.5, 28.5) * mm});
            skLineSegment(sketch, "E101.1", {"start": v(-111.5, 28.5) * mm, "end": v(-118.5, 28.5) * mm});
            skLineSegment(sketch, "E101.2", {"start": v(-118.5, 10) * mm, "end": v(-118.5, 28.5) * mm});
            skArc(sketch, "E102.0", {"start": v(-106.4, 18.89) * mm, "mid": v(-100.45, 13.52) * mm, "end": v(-93.81, 18) * mm});
            skArc(sketch, "E102.1", {"start": v(-111.5, 22) * mm, "mid": v(-109.83, 19.02) * mm, "end": v(-106.4, 18.89) * mm});
            skArc(sketch, "E103.0", {"start": v(-91.15, 17.93) * mm, "mid": v(-92.46, 18.78) * mm, "end": v(-93.81, 18) * mm});
            skArc(sketch, "E104.0", {"start": v(-76.15, 17.93) * mm, "mid": v(-77.46, 18.78) * mm, "end": v(-78.81, 18) * mm});
            skArc(sketch, "E104.1", {"start": v(-91.23, 18.15) * mm, "mid": v(-85.07, 13.5) * mm, "end": v(-78.81, 18) * mm});
            skArc(sketch, "E105.0", {"start": v(-46.15, 17.93) * mm, "mid": v(-47.46, 18.78) * mm, "end": v(-48.81, 18) * mm});
            skArc(sketch, "E105.1", {"start": v(-61.19, 18) * mm, "mid": v(-55, 13.5) * mm, "end": v(-48.81, 18) * mm});
            skArc(sketch, "E105.2", {"start": v(-61.19, 18) * mm, "mid": v(-62.5, 18.78) * mm, "end": v(-63.81, 18) * mm});
            skArc(sketch, "E105.3", {"start": v(-76.23, 18.15) * mm, "mid": v(-70.07, 13.5) * mm, "end": v(-63.81, 18) * mm});
            skLineSegment(sketch, "E106.0", {"start": v(-18.5, 60) * mm, "end": v(-18.5, 20) * mm});
            skArc(sketch, "E106.1", {"start": v(-31.19, 18) * mm, "mid": v(-24, 13.58) * mm, "end": v(-18.5, 20) * mm});
            skArc(sketch, "E106.2", {"start": v(-31.19, 18) * mm, "mid": v(-32.5, 18.78) * mm, "end": v(-33.81, 18) * mm});
            skArc(sketch, "E106.3", {"start": v(-46.23, 18.15) * mm, "mid": v(-40.07, 13.5) * mm, "end": v(-33.81, 18) * mm});
            skArc(sketch, "E107.0", {"start": v(-110, 88.5) * mm, "mid": v(-116.01, 86.01) * mm, "end": v(-118.5, 80) * mm});
            skArc(sketch, "E107.1", {"start": v(-18.51, 59.8) * mm, "mid": v(-21.42, 68.5) * mm, "end": v(-30.1, 71.5) * mm});
            skLineSegment(sketch, "E107.2", {"start": v(-30.1, 71.5) * mm, "end": v(-118, 71.5) * mm});
            skArc(sketch, "E107.3", {"start": v(-118.5, 72) * mm, "mid": v(-118.35, 71.65) * mm, "end": v(-118, 71.5) * mm});
            skLineSegment(sketch, "E107.4", {"start": v(-118.5, 80) * mm, "end": v(-118.5, 72) * mm});
            skSolve(sketch);
        }
        {
            var Q0;
            Q0 = qSketchRegion(id + "F13", true);
            extrude(context, id + "F14", {"entities" : qUnion([Q0]), "operationType" : NewBodyOperationType.ADD, "depth" : 3 * mm, "offsetDistance" : 25 * mm});
        }
        {
            var Q0;
            Q0=makeQuery(id+"F14.opExtrude","SWEPT_EDGE",EDGE,{"disambiguationData":[OSD([sQuery(id+"F13.wireOp",EDGE,"E101.1"),sQuery(id+"F13.wireOp",EDGE,"E101.2")])]});
            var Q1;
            Q1=makeQuery(id+"F14.opExtrude","SWEPT_EDGE",EDGE,{"disambiguationData":[OSD([sQuery(id+"F13.wireOp",EDGE,"E101.0"),sQuery(id+"F13.wireOp",EDGE,"E101.1")])]});
            fillet(context, id + "F15", {"entities" : qUnion([Q0, Q1]), "radius" : 1 * mm, "tangentPropagation" : true, "allowEdgeOverflow" : false});
        }
        {
            var Q0;
            Q0=makeQuery(id+"F1.opExtrude","CAP_FACE",FACE,{"disambiguationData":[OSD([sQuery(id+"F0.wireOp",EDGE,"E0"),sQuery(id+"F0.wireOp",EDGE,"E1"),sQuery(id+"F0.wireOp",EDGE,"E2"),sQuery(id+"F0.wireOp",EDGE,"E3"),sQuery(id+"F0.wireOp",EDGE,"E4"),sQuery(id+"F0.wireOp",EDGE,"E5"),sQuery(id+"F0.wireOp",EDGE,"E6"),sQuery(id+"F0.wireOp",EDGE,"E7"),sQuery(id+"F0.wireOp",EDGE,"E8"),sQuery(id+"F0.wireOp",EDGE,"E10"),sQuery(id+"F0.wireOp",EDGE,"E11"),sQuery(id+"F0.wireOp",EDGE,"E12"),sQuery(id+"F0.wireOp",EDGE,"E13"),sQuery(id+"F0.wireOp",EDGE,"E14"),sQuery(id+"F0.wireOp",EDGE,"E15"),sQuery(id+"F0.wireOp",EDGE,"E16"),sQuery(id+"F0.wireOp",EDGE,"E17"),sQuery(id+"F0.wireOp",EDGE,"E18"),sQuery(id+"F0.wireOp",EDGE,"E19"),sQuery(id+"F0.wireOp",EDGE,"E20"),sQuery(id+"F0.wireOp",EDGE,"E21")])],"isStart":true});
            var sketch = newSketch(context, id + "F16", { "sketchPlane" : qUnion([Q0])});
            skArc(sketch, "E108", {"start": v(31.7, 20) * mm, "mid": v(30.51, 19.6) * mm, "end": v(29.8, 18.58) * mm});
            skArc(sketch, "E109", {"start": v(35.2, 18.58) * mm, "mid": v(34.49, 19.6) * mm, "end": v(33.3, 20) * mm});
            skLineSegment(sketch, "E110", {"start": v(31.7, 20) * mm, "end": v(33.3, 20) * mm});
            skArc(sketch, "E111", {"start": v(46.7, 20) * mm, "mid": v(45.51, 19.6) * mm, "end": v(44.8, 18.58) * mm});
            skArc(sketch, "E112", {"start": v(50.2, 18.57) * mm, "mid": v(49.49, 19.6) * mm, "end": v(48.3, 20) * mm});
            skLineSegment(sketch, "E113", {"start": v(48.3, 20) * mm, "end": v(46.7, 20) * mm});
            skLineSegment(sketch, "E114", {"start": v(35.2, 18.58) * mm, "end": v(44.8, 18.58) * mm});
            skArc(sketch, "E115", {"start": v(61.7, 20) * mm, "mid": v(60.51, 19.6) * mm, "end": v(59.8, 18.57) * mm});
            skArc(sketch, "E116", {"start": v(65.2, 18.57) * mm, "mid": v(64.49, 19.6) * mm, "end": v(63.3, 20) * mm});
            skLineSegment(sketch, "E117", {"start": v(50.2, 18.57) * mm, "end": v(59.8, 18.57) * mm});
            skLineSegment(sketch, "E118", {"start": v(61.7, 20) * mm, "end": v(63.3, 20) * mm});
            skArc(sketch, "E119", {"start": v(76.7, 20) * mm, "mid": v(75.51, 19.6) * mm, "end": v(74.8, 18.57) * mm});
            skArc(sketch, "E120", {"start": v(80.2, 18.57) * mm, "mid": v(79.49, 19.6) * mm, "end": v(78.3, 20) * mm});
            skLineSegment(sketch, "E121", {"start": v(76.7, 20) * mm, "end": v(78.3, 20) * mm});
            skArc(sketch, "E122", {"start": v(91.7, 20) * mm, "mid": v(90.51, 19.6) * mm, "end": v(89.8, 18.57) * mm});
            skArc(sketch, "E123", {"start": v(95.2, 18.57) * mm, "mid": v(94.49, 19.6) * mm, "end": v(93.3, 20) * mm});
            skLineSegment(sketch, "E124", {"start": v(93.3, 20) * mm, "end": v(91.7, 20) * mm});
            skLineSegment(sketch, "E125", {"start": v(95.2, 18.57) * mm, "end": v(96.52, 20) * mm});
            skLineSegment(sketch, "E126", {"start": v(96.52, 20) * mm, "end": v(92.66, 22.23) * mm});
            skLineSegment(sketch, "E127", {"start": v(65.2, 18.57) * mm, "end": v(74.8, 18.57) * mm});
            skLineSegment(sketch, "E128", {"start": v(80.2, 18.57) * mm, "end": v(89.8, 18.57) * mm});
            skLineSegment(sketch, "E129", {"start": v(29.8, 18.58) * mm, "end": v(24.15, 27.7) * mm});
            skLineSegment(sketch, "E130", {"start": v(24.15, 27.7) * mm, "end": v(92.66, 22.23) * mm});
            skSolve(sketch);
        }
        {
            var Q0;
            Q0 = qSketchRegion(id + "F16", true);
            extrude(context, id + "F17", {"entities" : qUnion([Q0]), "operationType" : NewBodyOperationType.REMOVE, "oppositeDirection" : true, "depth" : 25 * mm, "offsetDistance" : 25 * mm});
        }
        {
            var Q0;
            Q0=makeQuery(id+"F12.opExtrude","CAP_EDGE",EDGE,{"disambiguationData":[OSD([sQuery(id+"F11.wireOp",EDGE,"E56")])],"isStart":true});
            var Q1;
            Q1=makeQuery(id+"F12.opExtrude","CAP_EDGE",EDGE,{"disambiguationData":[OSD([sQuery(id+"F11.wireOp",EDGE,"E57.0")])],"isStart":true});
            var Q2;
            Q2=makeQuery(id+"F12.opExtrude","CAP_EDGE",EDGE,{"disambiguationData":[OSD([sQuery(id+"F11.wireOp",EDGE,"E53.0")])],"isStart":true});
            var Q3;
            Q3=makeQuery(id+"F12.opExtrude","CAP_EDGE",EDGE,{"disambiguationData":[OSD([sQuery(id+"F11.wireOp",EDGE,"E52")])],"isStart":true});
            var Q4;
            Q4=makeQuery(id+"F12.opExtrude","CAP_EDGE",EDGE,{"disambiguationData":[OSD([sQuery(id+"F11.wireOp",EDGE,"E60.left")])],"isStart":true});
            var Q5;
            Q5=makeQuery(id+"F12.opExtrude","CAP_EDGE",EDGE,{"disambiguationData":[OSD([sQuery(id+"F11.wireOp",EDGE,"E60.right")])],"isStart":true});
            fillet(context, id + "F18", {"entities" : qUnion([Q0, Q1, Q2, Q3, Q4, Q5]), "radius" : 1 * mm, "tangentPropagation" : true, "allowEdgeOverflow" : false});
        }
        {
            var Q0;
            {var subQ0=sQuery(id+"F0.wireOp",EDGE,"E1");var subQ1=sQuery(id+"F0.wireOp",EDGE,"E21");var subQ2=sQuery(id+"F0.wireOp",EDGE,"E20");var subQ3=sQuery(id+"F0.wireOp",EDGE,"E19");var subQ4=sQuery(id+"F0.wireOp",EDGE,"E18");var subQ5=sQuery(id+"F0.wireOp",EDGE,"E17");var subQ6=sQuery(id+"F0.wireOp",EDGE,"E16");var subQ7=sQuery(id+"F0.wireOp",EDGE,"E15");var subQ8=sQuery(id+"F0.wireOp",EDGE,"E14");var subQ9=sQuery(id+"F0.wireOp",EDGE,"E13");var subQ10=sQuery(id+"F0.wireOp",EDGE,"E12");var subQ11=sQuery(id+"F0.wireOp",EDGE,"E11");var subQ12=sQuery(id+"F0.wireOp",EDGE,"E10");var subQ13=sQuery(id+"F0.wireOp",EDGE,"E8");var subQ14=sQuery(id+"F0.wireOp",EDGE,"E7");var subQ15=sQuery(id+"F0.wireOp",EDGE,"E6");var subQ16=sQuery(id+"F0.wireOp",EDGE,"E5");var subQ17=sQuery(id+"F0.wireOp",EDGE,"E4");var subQ18=sQuery(id+"F0.wireOp",EDGE,"E3");var subQ19=sQuery(id+"F0.wireOp",EDGE,"E2");var subQ20=sQuery(id+"F0.wireOp",EDGE,"E0");Q0=makeQuery(id+"F12.boolean.opBoolean","SPLIT",FACE,{"disambiguationData":[TD([makeQuery(id+"F9.opFillet","BLEND_FACE",FACE,{"disambiguationData":[OSD([subQ19])]})])],"derivedFrom":makeQuery(id+"F7.opShell","OFFSET_FACE",FACE,{"disambiguationData":[OSD([subQ20,subQ0,subQ19,subQ18,subQ17,subQ16,subQ15,subQ14,subQ13,subQ12,subQ11,subQ10,subQ9,subQ8,subQ7,subQ6,subQ5,subQ4,subQ3,subQ2,subQ1])]})});}
            var sketch = newSketch(context, id + "F19", { "sketchPlane" : qUnion([Q0])});
            skLineSegment(sketch, "E131.bottom", {"start": v(-110, 80) * mm, "end": v(-12, 80) * mm, "construction": true});
            skLineSegment(sketch, "E131.top", {"start": v(-110, 8.5) * mm, "end": v(-12, 8.5) * mm, "construction": true});
            skLineSegment(sketch, "E131.left", {"start": v(-110, 80) * mm, "end": v(-110, 8.5) * mm, "construction": true});
            skLineSegment(sketch, "E131.right", {"start": v(-12, 80) * mm, "end": v(-12, 8.5) * mm, "construction": true});
            skCircle(sketch, "E132", {"center": v(-110, 80) * mm, "radius": 3 * mm});
            skCircle(sketch, "E133", {"center": v(-12, 80) * mm, "radius": 3 * mm});
            skCircle(sketch, "E134", {"center": v(-12, 8.5) * mm, "radius": 3 * mm});
            skCircle(sketch, "E135", {"center": v(-110, 8.5) * mm, "radius": 3 * mm});
            skSolve(sketch);
        }
        {
            var Q0;
            Q0 = qSketchRegion(id + "F19", true);
            extrude(context, id + "F20", {"entities" : qUnion([Q0]), "operationType" : NewBodyOperationType.ADD, "depth" : 9.5 * mm, "offsetDistance" : 25 * mm});
        }
        {
            var Q0;
            Q0=makeQuery(id+"F20.opExtrude","CAP_EDGE",EDGE,{"disambiguationData":[OSD([sQuery(id+"F19.wireOp",EDGE,"E135")])],"isStart":true});
            var Q1;
            {var subQ0=sQuery(id+"F19.wireOp",EDGE,"E134");Q1=makeQuery(id+"F20.boolean.opBoolean","SPLIT",EDGE,{"disambiguationData":[TD([makeQuery(id+"F18.opFillet","BLEND_FACE",FACE,{"disambiguationData":[OSD([sQuery(id+"F11.wireOp",EDGE,"E52")]),OD(1.0)]})])],"derivedFrom":makeQuery(id+"F20.opExtrude","CAP_EDGE",EDGE,{"disambiguationData":[OSD([subQ0])],"isStart":true})});}
            var Q2;
            Q2=makeQuery(id+"F20.boolean.opBoolean","INTERSECT",EDGE,{"disambiguationData":[OD(1.0)],"derivedFrom":[makeQuery(id+"F12.opExtrude","SWEPT_FACE",FACE,{"disambiguationData":[OSD([sQuery(id+"F11.wireOp",EDGE,"E52")])]}),makeQuery(id+"F20.opExtrude","SWEPT_FACE",FACE,{"disambiguationData":[OSD([sQuery(id+"F19.wireOp",EDGE,"E134")])]})]});
            var Q3;
            Q3=makeQuery(id+"F20.opExtrude","CAP_EDGE",EDGE,{"disambiguationData":[OSD([sQuery(id+"F19.wireOp",EDGE,"E133")])],"isStart":true});
            var Q4;
            Q4=makeQuery(id+"F20.opExtrude","CAP_EDGE",EDGE,{"disambiguationData":[OSD([sQuery(id+"F19.wireOp",EDGE,"E132")])],"isStart":true});
            var Q5;
            {var subQ0=sQuery(id+"F19.wireOp",EDGE,"E134");Q5=makeQuery(id+"F20.boolean.opBoolean","SPLIT",EDGE,{"disambiguationData":[TD([makeQuery(id+"F18.opFillet","BLEND_FACE",FACE,{"disambiguationData":[OSD([sQuery(id+"F11.wireOp",EDGE,"E53.0")])]})])],"derivedFrom":makeQuery(id+"F20.opExtrude","CAP_EDGE",EDGE,{"disambiguationData":[OSD([subQ0])],"isStart":true})});}
            var Q6;
            Q6=makeQuery(id+"F20.boolean.opBoolean","INTERSECT",EDGE,{"disambiguationData":[OD(1.0)],"derivedFrom":[makeQuery(id+"F12.opExtrude","SWEPT_FACE",FACE,{"disambiguationData":[OSD([sQuery(id+"F11.wireOp",EDGE,"E53.0")])]}),makeQuery(id+"F20.opExtrude","SWEPT_FACE",FACE,{"disambiguationData":[OSD([sQuery(id+"F19.wireOp",EDGE,"E134")])]})]});
            fillet(context, id + "F21", {"entities" : qUnion([Q0, Q1, Q2, Q3, Q4, Q5, Q6]), "radius" : 1 * mm, "tangentPropagation" : true, "allowEdgeOverflow" : false});
        }
        {
            var Q0;
            Q0=makeQuery(id+"F20.opExtrude","CAP_FACE",FACE,{"disambiguationData":[OSD([sQuery(id+"F19.wireOp",EDGE,"E132")])],"isStart":false});
            var sketch = newSketch(context, id + "F22", { "sketchPlane" : qUnion([Q0])});
            skCircle(sketch, "E136.0", {"center": v(-110, 80) * mm, "radius": 1 * mm});
            skCircle(sketch, "E137.0", {"center": v(-12, 80) * mm, "radius": 1 * mm});
            skCircle(sketch, "E138.0", {"center": v(-110, 8.5) * mm, "radius": 1 * mm});
            skLineSegment(sketch, "E139.bottom", {"start": v(-110, 80) * mm, "end": v(-12, 80) * mm, "construction": true});
            skLineSegment(sketch, "E139.top", {"start": v(-110, 8.5) * mm, "end": v(-12, 8.5) * mm, "construction": true});
            skLineSegment(sketch, "E139.left", {"start": v(-110, 80) * mm, "end": v(-110, 8.5) * mm, "construction": true});
            skLineSegment(sketch, "E139.right", {"start": v(-12, 80) * mm, "end": v(-12, 8.5) * mm, "construction": true});
            skCircle(sketch, "E140", {"center": v(-12, 8.5) * mm, "radius": 1 * mm});
            skSolve(sketch);
        }
        {
            var Q0;
            Q0 = qSketchRegion(id + "F22", true);
            extrude(context, id + "F23", {"entities" : qUnion([Q0]), "operationType" : NewBodyOperationType.REMOVE, "oppositeDirection" : true, "depth" : 6 * mm, "offsetDistance" : 25 * mm});
        }
    });
